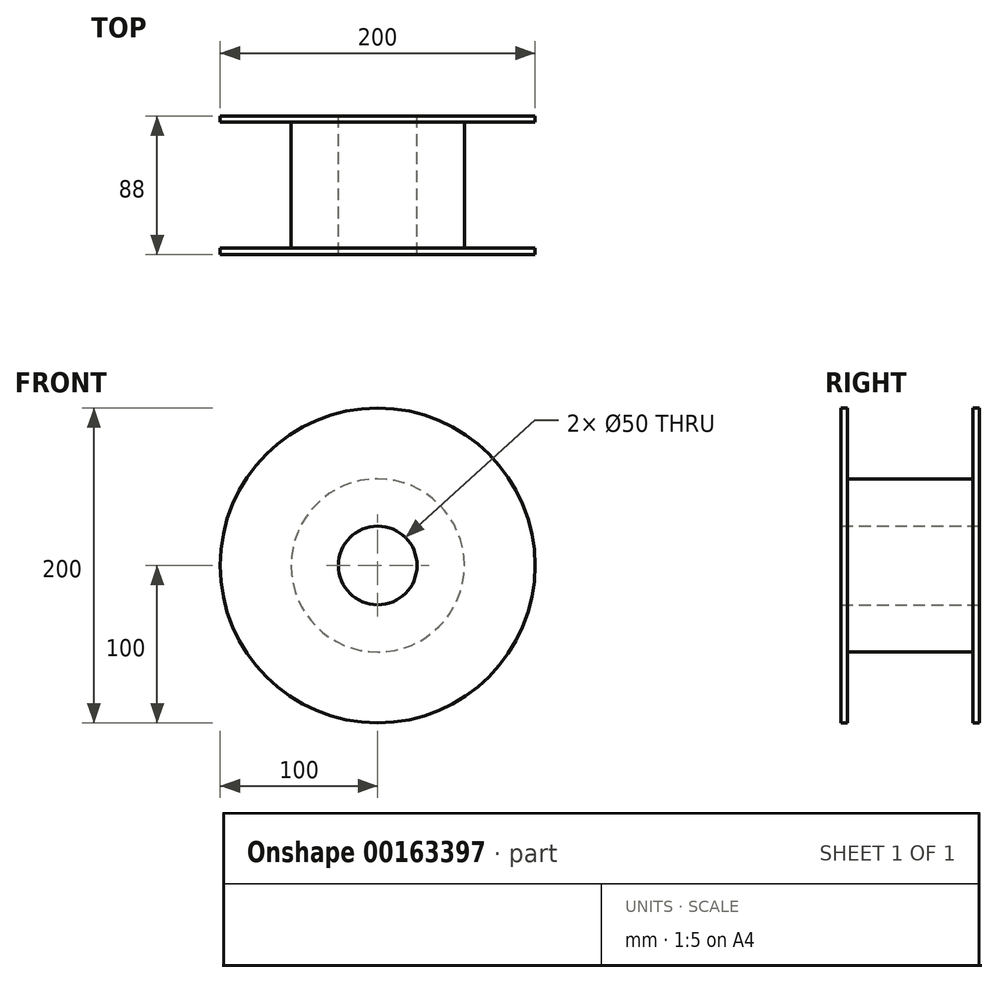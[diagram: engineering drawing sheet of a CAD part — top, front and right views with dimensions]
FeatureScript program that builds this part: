
annotation { "Feature Type Name" : "Feature", "Feature Type Description" : "" }
export const myFeature = defineFeature(function(context is Context, id is Id, definition is map)
    precondition{}
    {
        {
            var Q0;
            Q0=qCreatedBy(makeId("Front.planeOp"),FACE);
            var sketch = newSketch(context, id + "F0", { "sketchPlane" : qUnion([Q0])});
            skCircle(sketch, "E0", {"center": v(0, 0) * mm, "radius": 100 * mm});
            skSolve(sketch);
        }
        {
            var Q0;
            Q0=makeQuery(id+"F0.imprint","IMPRINT",FACE,{"disambiguationData":[TD([[makeQuery(id+"F0.imprint","IMPRINT",EDGE,{"derivedFrom":sQuery(id+"F0.wireOp",EDGE,"E0")}),1.0]])]});
            extrude(context, id + "F1", {"entities" : qUnion([Q0]), "depth" : 4 * mm});
        }
        {
            var Q0;
            Q0=makeQuery(id+"F1.opExtrude","CAP_FACE",FACE,{"disambiguationData":[OSD([sQuery(id+"F0.wireOp",EDGE,"E0")])],"isStart":true});
            var sketch = newSketch(context, id + "F2", { "sketchPlane" : qUnion([Q0])});
            skCircle(sketch, "E1", {"center": v(0, 0) * mm, "radius": 55 * mm});
            skSolve(sketch);
        }
        {
            var Q0;
            Q0=makeQuery(id+"F2.imprint","IMPRINT",FACE,{"disambiguationData":[TD([[makeQuery(id+"F2.imprint","IMPRINT",EDGE,{"derivedFrom":sQuery(id+"F2.wireOp",EDGE,"E1")}),1.0]])]});
            var Q1;
            Q1=sQuery(id+"F2.wireOp",EDGE,"E1");
            extrude(context, id + "F3", {"entities" : qUnion([Q0]), "operationType" : NewBodyOperationType.ADD, "surfaceEntities" : qUnion([Q1]), "depth" : 84 * mm});
        }
        {
            var Q0;
            Q0=makeQuery(id+"F3.opExtrude","CAP_FACE",FACE,{"disambiguationData":[OSD([sQuery(id+"F2.wireOp",EDGE,"E1")])],"isStart":false});
            var sketch = newSketch(context, id + "F4", { "sketchPlane" : qUnion([Q0])});
            skCircle(sketch, "E2", {"center": v(0, 0) * mm, "radius": 100 * mm});
            skSolve(sketch);
        }
        {
            var Q0;
            Q0=makeQuery(id+"F4.imprint","IMPRINT",FACE,{"disambiguationData":[TD([[makeQuery(id+"F4.imprint","IMPRINT",EDGE,{"derivedFrom":sQuery(id+"F4.wireOp",EDGE,"E2")}),1.0]])]});
            extrude(context, id + "F5", {"entities" : qUnion([Q0]), "oppositeDirection" : true, "depth" : 4 * mm});
        }
        {
            var Q0;
            Q0=makeQuery(id+"F3.opExtrude","CAP_FACE",FACE,{"disambiguationData":[OSD([sQuery(id+"F2.wireOp",EDGE,"E1")])],"isStart":false});
            var sketch = newSketch(context, id + "F6", { "sketchPlane" : qUnion([Q0])});
            skCircle(sketch, "E3", {"center": v(0, 0) * mm, "radius": 25 * mm});
            skSolve(sketch);
        }
        {
            var Q0;
            Q0=makeQuery(id+"F6.imprint","IMPRINT",FACE,{"disambiguationData":[TD([[makeQuery(id+"F6.imprint","IMPRINT",EDGE,{"derivedFrom":sQuery(id+"F6.wireOp",EDGE,"E3")}),1.0]])]});
            var Q1;
            Q1=sQuery(id+"F6.wireOp",EDGE,"E3");
            var Q2;
            Q2=makeQuery(id+"F1.opExtrude","CAP_FACE",FACE,{"disambiguationData":[OSD([sQuery(id+"F0.wireOp",EDGE,"E0")])],"isStart":false});
            extrude(context, id + "F7", {"entities" : qUnion([Q0]), "operationType" : NewBodyOperationType.REMOVE, "surfaceEntities" : qUnion([Q1]), "endBound" : BoundingType.UP_TO_SURFACE, "oppositeDirection" : true, "endBoundEntityFace" : qUnion([Q2]), "depth" : 25 * mm});
        }
    });
